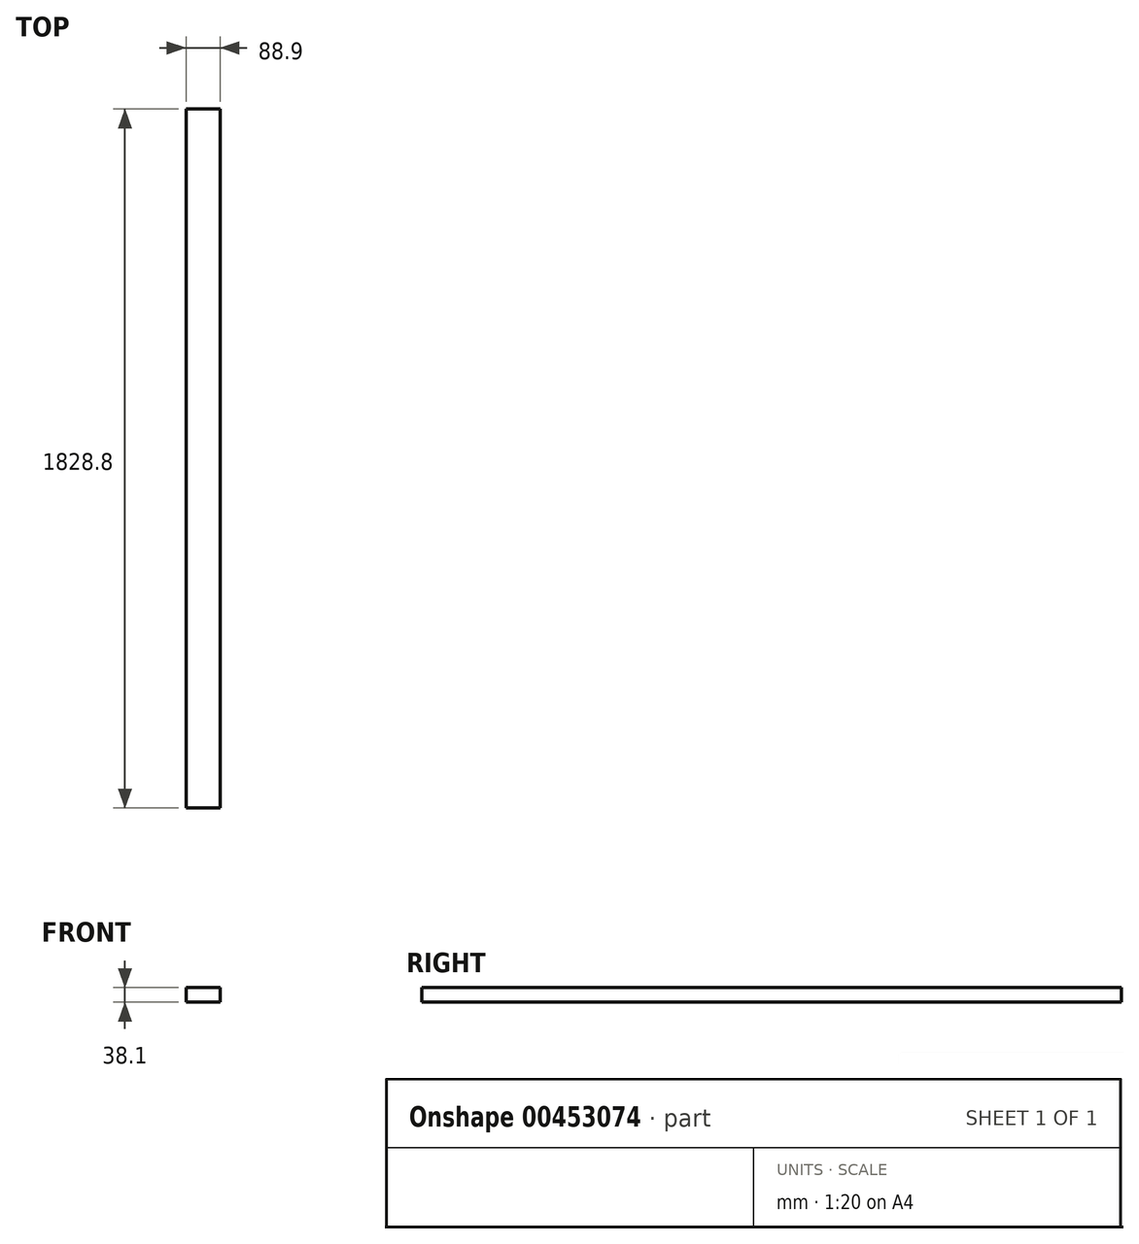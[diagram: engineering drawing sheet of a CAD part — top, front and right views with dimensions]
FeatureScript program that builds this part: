
annotation { "Feature Type Name" : "Feature", "Feature Type Description" : "" }
export const myFeature = defineFeature(function(context is Context, id is Id, definition is map)
    precondition{}
    {
        {
            var Q0;
            Q0=qCreatedBy(makeId("Front.planeOp"),FACE);
            var sketch = newSketch(context, id + "F0", { "sketchPlane" : qUnion([Q0])});
            skLineSegment(sketch, "E0.bottom", {"start": v(44.45, 19.05) * mm, "end": v(-44.45, 19.05) * mm});
            skLineSegment(sketch, "E0.top", {"start": v(44.45, -19.05) * mm, "end": v(-44.45, -19.05) * mm});
            skLineSegment(sketch, "E0.left", {"start": v(44.45, 19.05) * mm, "end": v(44.45, -19.05) * mm});
            skLineSegment(sketch, "E0.right", {"start": v(-44.45, 19.05) * mm, "end": v(-44.45, -19.05) * mm});
            skPoint(sketch, "E0.middle", {"position": v(0, 0) * mm});
            skSolve(sketch);
        }
        {
            var Q0;
            Q0 = qSketchRegion(id + "F0", true);
            extrude(context, id + "F1", {"entities" : qUnion([Q0]), "depth" : 1828.8 * mm, "offsetDistance" : 25.4 * mm});
        }
    });
